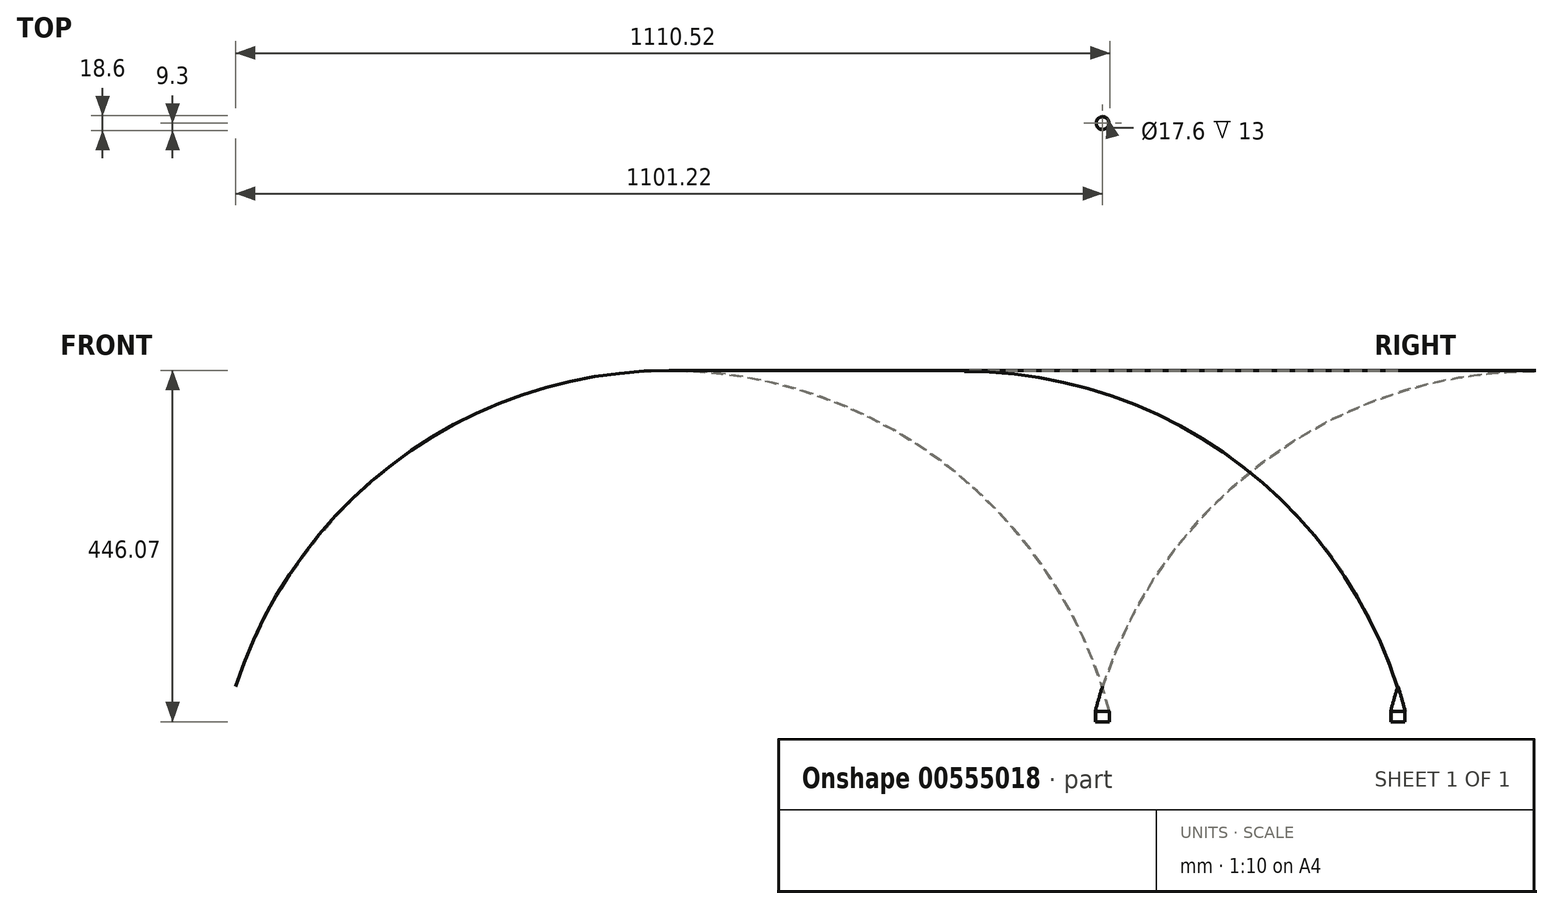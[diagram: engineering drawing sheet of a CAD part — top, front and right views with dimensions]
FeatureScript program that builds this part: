
annotation { "Feature Type Name" : "Feature", "Feature Type Description" : "" }
export const myFeature = defineFeature(function(context is Context, id is Id, definition is map)
    precondition{}
    {
        {
            var Q0;
            Q0=qCreatedBy(makeId("Front.planeOp"),FACE);
            var sketch = newSketch(context, id + "F0", { "sketchPlane" : qUnion([Q0])});
            skLineSegment(sketch, "E0", {"start": v(0, 0) * mm, "end": v(0, 70) * mm});
            skLineSegment(sketch, "E1", {"start": v(7.8, 25) * mm, "end": v(7.8, 39) * mm});
            skLineSegment(sketch, "E2", {"start": v(7.8, 39) * mm, "end": v(8, 39) * mm});
            skArc(sketch, "E3", {"start": v(8, 39) * mm, "mid": v(4.18, 52.9) * mm, "end": v(0, 66.71) * mm});
            skArc(sketch, "E4.0", {"start": v(9.3, 38) * mm, "mid": v(4.88, 54.07) * mm, "end": v(0, 70) * mm});
            skLineSegment(sketch, "E4.1", {"start": v(8.8, 38) * mm, "end": v(9.3, 38) * mm});
            skLineSegment(sketch, "E4.2", {"start": v(8.8, 25) * mm, "end": v(8.8, 38) * mm});
            skLineSegment(sketch, "E5", {"start": v(7.8, 25) * mm, "end": v(8.8, 25) * mm});
            skSolve(sketch);
        }
        {
            var Q0;
            Q0=makeQuery(id+"F0.imprint","IMPRINT",FACE,{"disambiguationData":[TD([[makeQuery(id+"F0.imprint","IMPRINT",EDGE,{"derivedFrom":sQuery(id+"F0.wireOp",EDGE,"E1")}),-1.0]])]});
            var Q1;
            Q1=sQuery(id+"F0.wireOp",EDGE,"E0");
            revolve(context, id + "F1", {"entities" : qUnion([Q0]), "axis" : qUnion([Q1]), "revolveType" : RevolveType.FULL});
        }
    });
